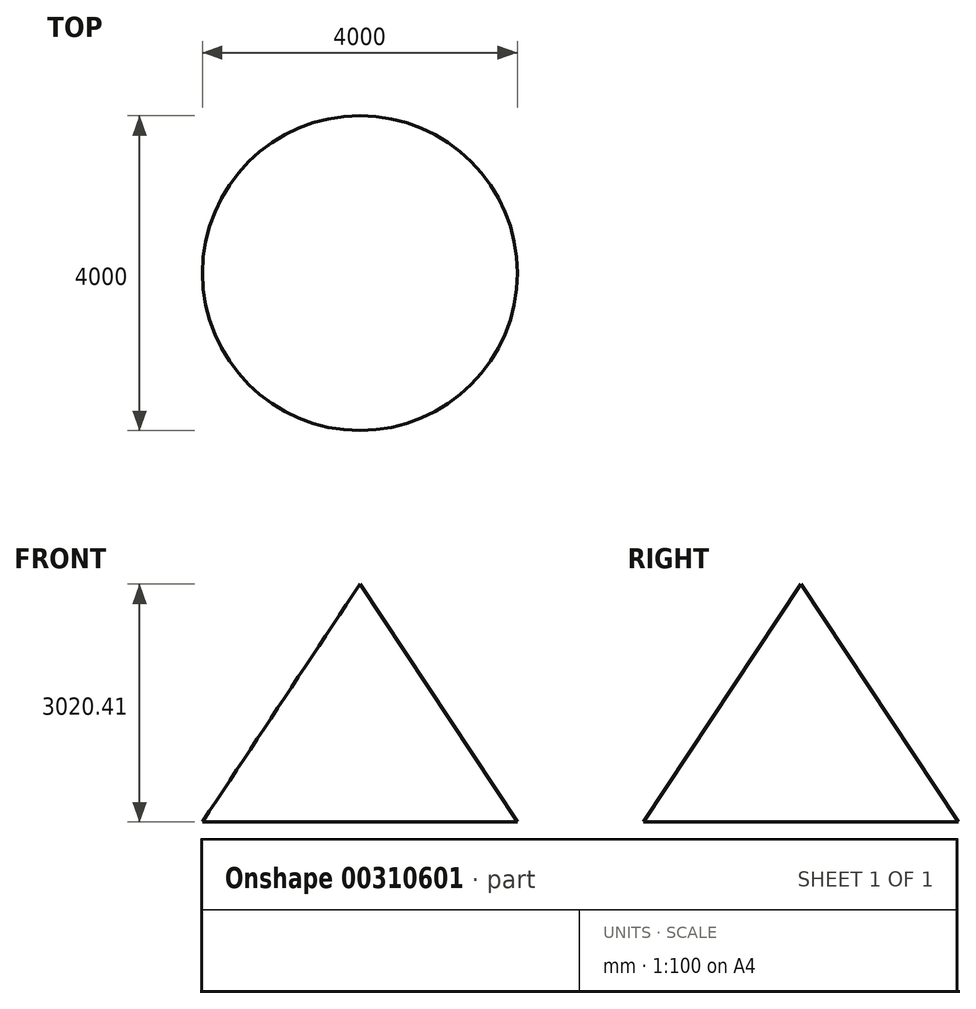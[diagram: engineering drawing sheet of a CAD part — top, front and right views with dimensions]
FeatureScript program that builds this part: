
annotation { "Feature Type Name" : "Feature", "Feature Type Description" : "" }
export const myFeature = defineFeature(function(context is Context, id is Id, definition is map)
    precondition{}
    {
        {
            var Q0;
            Q0=qCreatedBy(makeId("Front.planeOp"),FACE);
            var sketch = newSketch(context, id + "F0", { "sketchPlane" : qUnion([Q0])});
            skLineSegment(sketch, "E0", {"start": v(0, 1954.08) * mm, "end": v(2000, -1066.33) * mm});
            skLineSegment(sketch, "E1", {"start": v(2000, -1066.33) * mm, "end": v(0, -1066.33) * mm});
            skLineSegment(sketch, "E2", {"start": v(0, -1066.33) * mm, "end": v(0, 1954.08) * mm});
            skLineSegment(sketch, "E3", {"start": v(0, 2188.78) * mm, "end": v(0, -1688.78) * mm, "construction": true});
            skSolve(sketch);
        }
        {
            var Q0;
            Q0=makeQuery(id+"F0.imprint","IMPRINT",FACE,{"disambiguationData":[TD([[makeQuery(id+"F0.imprint","IMPRINT",EDGE,{"derivedFrom":sQuery(id+"F0.wireOp",EDGE,"E0")}),-1.0]])]});
            var Q1;
            Q1=sQuery(id+"F0.wireOp",EDGE,"E3");
            revolve(context, id + "F1", {"entities" : qUnion([Q0]), "axis" : qUnion([Q1]), "revolveType" : RevolveType.FULL});
        }
    });
